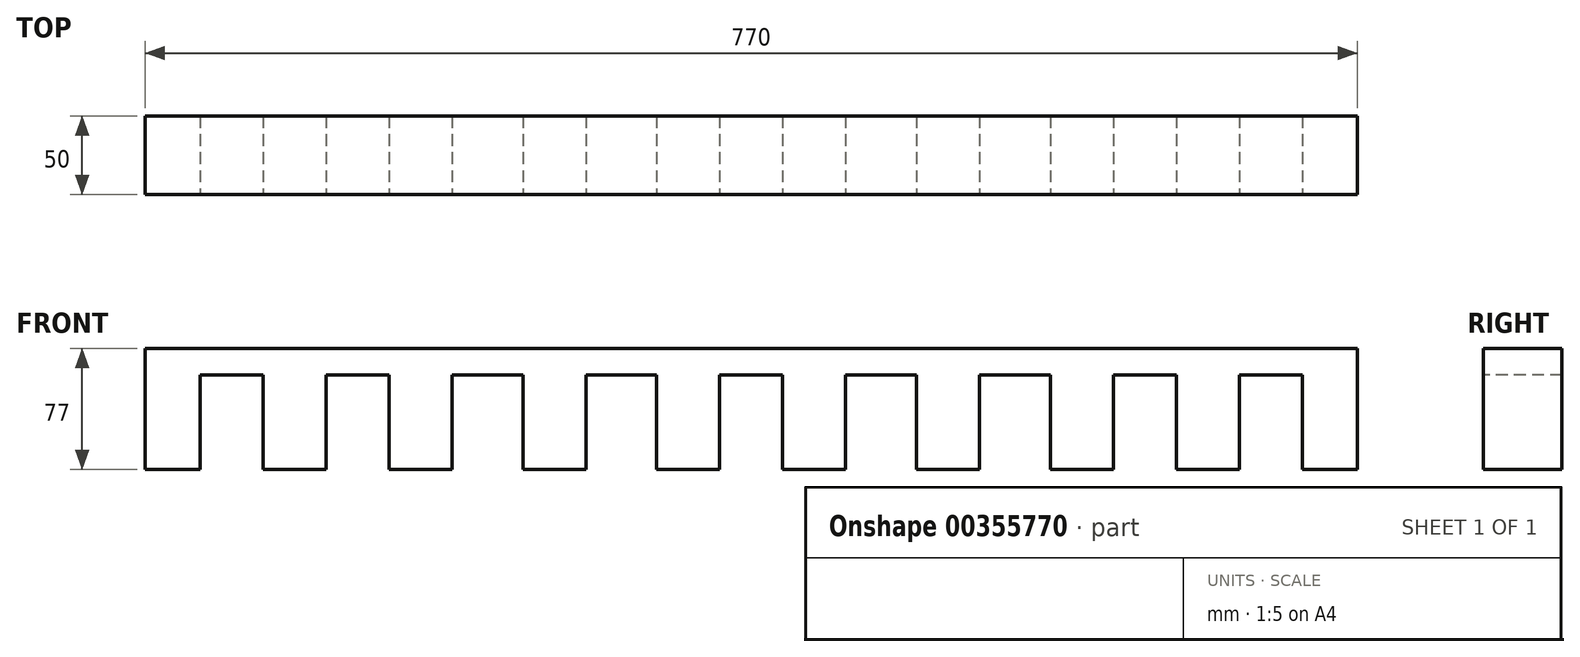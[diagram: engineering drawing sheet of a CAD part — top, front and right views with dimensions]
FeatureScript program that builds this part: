
annotation { "Feature Type Name" : "Feature", "Feature Type Description" : "" }
export const myFeature = defineFeature(function(context is Context, id is Id, definition is map)
    precondition{}
    {
        {
            var Q0;
            Q0=qCreatedBy(makeId("Front.planeOp"),FACE);
            var sketch = newSketch(context, id + "F0", { "sketchPlane" : qUnion([Q0])});
            skLineSegment(sketch, "E0.bottom", {"start": v(-404.78, 0) * mm, "end": v(375.22, 0) * mm});
            skLineSegment(sketch, "E0.top", {"start": v(-404.78, -80) * mm, "end": v(375.22, -80) * mm});
            skLineSegment(sketch, "E0.left", {"start": v(-404.78, 0) * mm, "end": v(-404.78, -80) * mm});
            skLineSegment(sketch, "E0.right", {"start": v(375.22, 0) * mm, "end": v(375.22, -80) * mm});
            skSolve(sketch);
        }
        {
            var Q0;
            Q0=makeQuery(id+"F0.imprint","IMPRINT",FACE,{"disambiguationData":[TD([[makeQuery(id+"F0.imprint","IMPRINT",EDGE,{"derivedFrom":sQuery(id+"F0.wireOp",EDGE,"E0.bottom")}),-1.0]])]});
            extrude(context, id + "F1", {"entities" : qUnion([Q0]), "depth" : 50 * mm});
        }
        {
            var Q0;
            Q0=makeQuery(id+"F1.opExtrude","CAP_FACE",FACE,{"disambiguationData":[OSD([sQuery(id+"F0.wireOp",EDGE,"E0.bottom"),sQuery(id+"F0.wireOp",EDGE,"E0.top"),sQuery(id+"F0.wireOp",EDGE,"E0.left"),sQuery(id+"F0.wireOp",EDGE,"E0.right")])],"isStart":false});
            var sketch = newSketch(context, id + "F2", { "sketchPlane" : qUnion([Q0])});
            skLineSegment(sketch, "E1.bottom", {"start": v(-364.78, -80) * mm, "end": v(-324.78, -80) * mm});
            skLineSegment(sketch, "E1.top", {"start": v(-364.78, -20) * mm, "end": v(-324.78, -20) * mm});
            skLineSegment(sketch, "E1.left", {"start": v(-364.78, -80) * mm, "end": v(-364.78, -20) * mm});
            skLineSegment(sketch, "E1.right", {"start": v(-324.78, -80) * mm, "end": v(-324.78, -20) * mm});
            skLineSegment(sketch, "E2.bottom", {"start": v(-284.78, -80) * mm, "end": v(-244.78, -80) * mm});
            skLineSegment(sketch, "E2.top", {"start": v(-284.78, -20) * mm, "end": v(-244.78, -20) * mm});
            skLineSegment(sketch, "E2.left", {"start": v(-284.78, -80) * mm, "end": v(-284.78, -20) * mm});
            skLineSegment(sketch, "E2.right", {"start": v(-244.78, -80) * mm, "end": v(-244.78, -20) * mm});
            skLineSegment(sketch, "E3.bottom", {"start": v(-204.78, -80) * mm, "end": v(-159.78, -80) * mm});
            skLineSegment(sketch, "E3.top", {"start": v(-204.78, -20) * mm, "end": v(-159.78, -20) * mm});
            skLineSegment(sketch, "E3.left", {"start": v(-204.78, -80) * mm, "end": v(-204.78, -20) * mm});
            skLineSegment(sketch, "E3.right", {"start": v(-159.78, -80) * mm, "end": v(-159.78, -20) * mm});
            skPoint(sketch, "E4.oppositeSnap0", {"position": v(-182.28, -20) * mm});
            skLineSegment(sketch, "E4.bottom", {"start": v(-119.78, -80) * mm, "end": v(-74.78, -80) * mm});
            skLineSegment(sketch, "E4.top", {"start": v(-119.78, -20) * mm, "end": v(-74.78, -20) * mm});
            skLineSegment(sketch, "E4.left", {"start": v(-119.78, -80) * mm, "end": v(-119.78, -20) * mm});
            skLineSegment(sketch, "E4.right", {"start": v(-74.78, -80) * mm, "end": v(-74.78, -20) * mm});
            skLineSegment(sketch, "E5.bottom", {"start": v(-34.78, -80) * mm, "end": v(5.22, -80) * mm});
            skLineSegment(sketch, "E5.top", {"start": v(-34.78, -20) * mm, "end": v(5.22, -20) * mm});
            skLineSegment(sketch, "E5.left", {"start": v(-34.78, -80) * mm, "end": v(-34.78, -20) * mm});
            skLineSegment(sketch, "E5.right", {"start": v(5.22, -80) * mm, "end": v(5.22, -20) * mm});
            skLineSegment(sketch, "E6.bottom", {"start": v(45.22, -80) * mm, "end": v(90.22, -80) * mm});
            skLineSegment(sketch, "E6.top", {"start": v(45.22, -20) * mm, "end": v(90.22, -20) * mm});
            skLineSegment(sketch, "E6.left", {"start": v(45.22, -80) * mm, "end": v(45.22, -20) * mm});
            skLineSegment(sketch, "E6.right", {"start": v(90.22, -80) * mm, "end": v(90.22, -20) * mm});
            skLineSegment(sketch, "E7.bottom", {"start": v(130.22, -80) * mm, "end": v(175.22, -80) * mm});
            skLineSegment(sketch, "E7.top", {"start": v(130.22, -20) * mm, "end": v(175.22, -20) * mm});
            skLineSegment(sketch, "E7.left", {"start": v(130.22, -80) * mm, "end": v(130.22, -20) * mm});
            skLineSegment(sketch, "E7.right", {"start": v(175.22, -80) * mm, "end": v(175.22, -20) * mm});
            skLineSegment(sketch, "E8.bottom", {"start": v(215.22, -80) * mm, "end": v(255.22, -80) * mm});
            skLineSegment(sketch, "E8.top", {"start": v(215.22, -20) * mm, "end": v(255.22, -20) * mm});
            skLineSegment(sketch, "E8.left", {"start": v(215.22, -80) * mm, "end": v(215.22, -20) * mm});
            skLineSegment(sketch, "E8.right", {"start": v(255.22, -80) * mm, "end": v(255.22, -20) * mm});
            skLineSegment(sketch, "E9.bottom", {"start": v(295.22, -80) * mm, "end": v(335.22, -80) * mm});
            skLineSegment(sketch, "E9.top", {"start": v(295.22, -20) * mm, "end": v(335.22, -20) * mm});
            skLineSegment(sketch, "E9.left", {"start": v(295.22, -80) * mm, "end": v(295.22, -20) * mm});
            skLineSegment(sketch, "E9.right", {"start": v(335.22, -80) * mm, "end": v(335.22, -20) * mm});
            skSolve(sketch);
        }
        {
            var Q0;
            Q0=qSketchRegion(id+"F2",true);
            extrude(context, id + "F3", {"entities" : qUnion([Q0]), "operationType" : NewBodyOperationType.REMOVE, "oppositeDirection" : true, "depth" : 50 * mm});
        }
        {
            var Q0;
            Q0=makeQuery(id+"F1.opExtrude","CAP_FACE",FACE,{"disambiguationData":[OSD([sQuery(id+"F0.wireOp",EDGE,"E0.bottom"),sQuery(id+"F0.wireOp",EDGE,"E0.top"),sQuery(id+"F0.wireOp",EDGE,"E0.left"),sQuery(id+"F0.wireOp",EDGE,"E0.right")])],"isStart":false});
            var sketch = newSketch(context, id + "F4", { "sketchPlane" : qUnion([Q0])});
            skLineSegment(sketch, "E10.bottom", {"start": v(-404.78, 0) * mm, "end": v(375.22, 0) * mm});
            skLineSegment(sketch, "E10.top", {"start": v(-404.78, -3) * mm, "end": v(375.22, -3) * mm});
            skLineSegment(sketch, "E10.left", {"start": v(-404.78, 0) * mm, "end": v(-404.78, -3) * mm});
            skLineSegment(sketch, "E10.right", {"start": v(375.22, 0) * mm, "end": v(375.22, -3) * mm});
            skSolve(sketch);
        }
        {
            var Q0;
            Q0 = qSketchRegion(id + "F4", true);
            extrude(context, id + "F5", {"entities" : qUnion([Q0]), "operationType" : NewBodyOperationType.REMOVE, "endBound" : BoundingType.UP_TO_NEXT, "oppositeDirection" : true, "depth" : 25 * mm, "offsetDistance" : 25 * mm});
        }
        {
            var Q0;
            Q0=makeQuery(id+"F1.opExtrude","CAP_FACE",FACE,{"disambiguationData":[OSD([sQuery(id+"F0.wireOp",EDGE,"E0.bottom"),sQuery(id+"F0.wireOp",EDGE,"E0.top"),sQuery(id+"F0.wireOp",EDGE,"E0.left"),sQuery(id+"F0.wireOp",EDGE,"E0.right")])],"isStart":false});
            var sketch = newSketch(context, id + "F6", { "sketchPlane" : qUnion([Q0])});
            skLineSegment(sketch, "E11.bottom", {"start": v(-404.78, -3) * mm, "end": v(-399.78, -3) * mm});
            skLineSegment(sketch, "E11.top", {"start": v(-404.78, -80) * mm, "end": v(-399.78, -80) * mm});
            skLineSegment(sketch, "E11.left", {"start": v(-404.78, -3) * mm, "end": v(-404.78, -80) * mm});
            skLineSegment(sketch, "E11.right", {"start": v(-399.78, -3) * mm, "end": v(-399.78, -80) * mm});
            skSolve(sketch);
        }
        {
            var Q0;
            Q0 = qSketchRegion(id + "F6", true);
            extrude(context, id + "F7", {"entities" : qUnion([Q0]), "operationType" : NewBodyOperationType.REMOVE, "endBound" : BoundingType.UP_TO_NEXT, "oppositeDirection" : true, "depth" : 25 * mm, "offsetDistance" : 25 * mm});
        }
        {
            var Q0;
            Q0=makeQuery(id+"F1.opExtrude","CAP_FACE",FACE,{"disambiguationData":[OSD([sQuery(id+"F0.wireOp",EDGE,"E0.bottom"),sQuery(id+"F0.wireOp",EDGE,"E0.top"),sQuery(id+"F0.wireOp",EDGE,"E0.left"),sQuery(id+"F0.wireOp",EDGE,"E0.right")])],"isStart":false});
            var sketch = newSketch(context, id + "F8", { "sketchPlane" : qUnion([Q0])});
            skLineSegment(sketch, "E12.bottom", {"start": v(375.22, -80) * mm, "end": v(370.22, -80) * mm});
            skLineSegment(sketch, "E12.top", {"start": v(375.22, -3) * mm, "end": v(370.22, -3) * mm});
            skLineSegment(sketch, "E12.left", {"start": v(375.22, -80) * mm, "end": v(375.22, -3) * mm});
            skLineSegment(sketch, "E12.right", {"start": v(370.22, -80) * mm, "end": v(370.22, -3) * mm});
            skSolve(sketch);
        }
        {
            var Q0;
            Q0 = qSketchRegion(id + "F8", true);
            extrude(context, id + "F9", {"entities" : qUnion([Q0]), "operationType" : NewBodyOperationType.REMOVE, "endBound" : BoundingType.UP_TO_NEXT, "oppositeDirection" : true, "depth" : 25 * mm, "offsetDistance" : 25 * mm});
        }
    });
